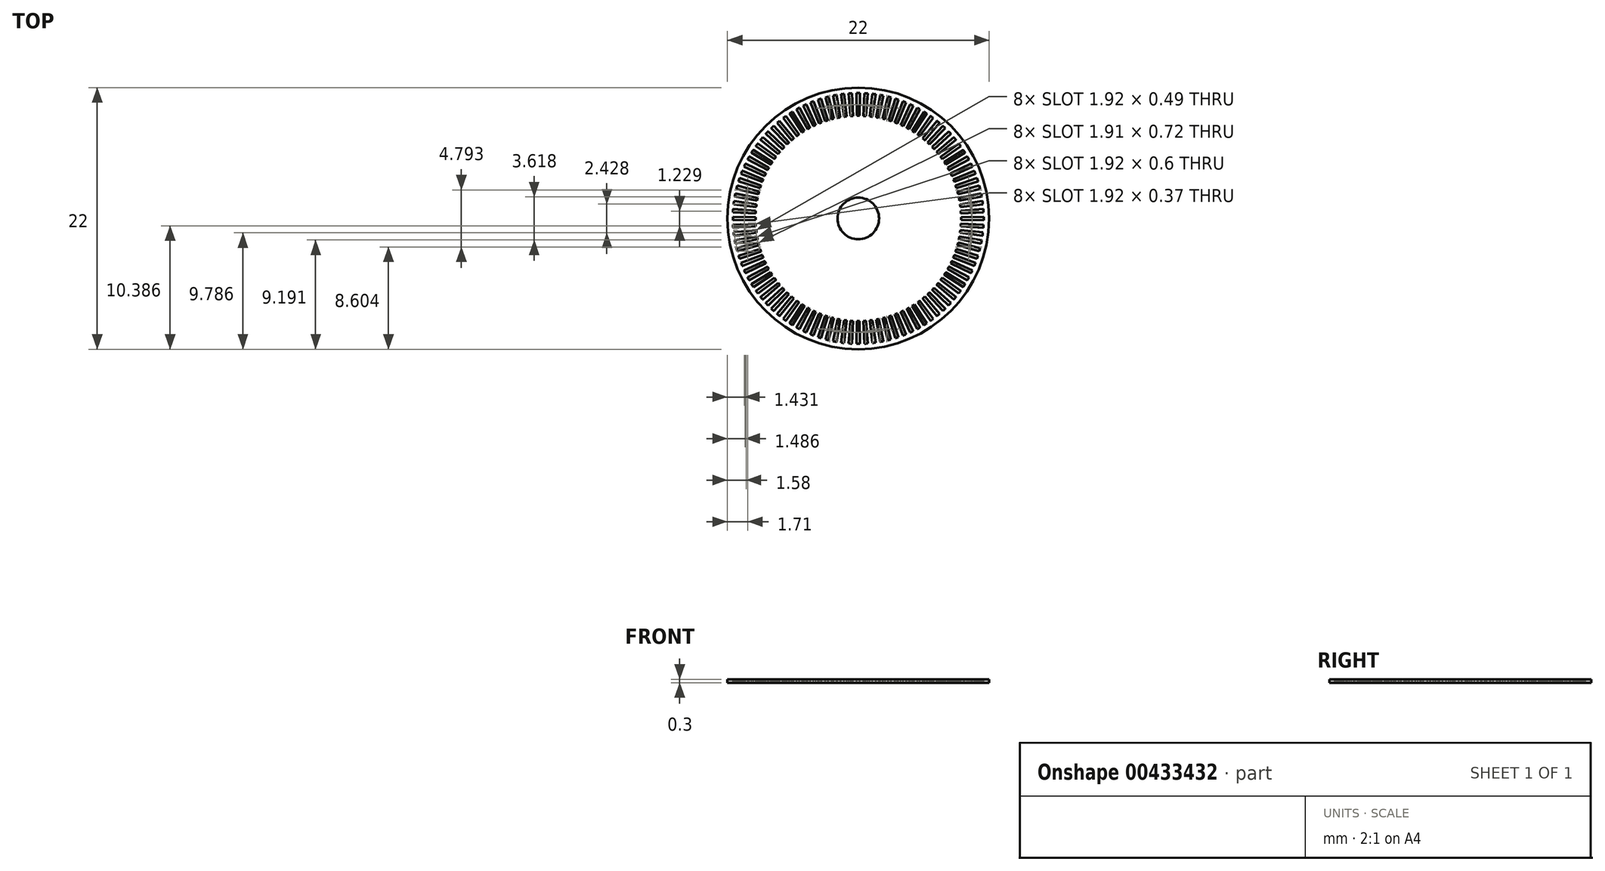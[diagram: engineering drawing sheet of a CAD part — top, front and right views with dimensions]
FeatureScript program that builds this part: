
annotation { "Feature Type Name" : "Feature", "Feature Type Description" : "" }
export const myFeature = defineFeature(function(context is Context, id is Id, definition is map)
    precondition{}
    {
        {
            var Q0;
            Q0=qCreatedBy(makeId("Top.planeOp"),FACE);
            var sketch = newSketch(context, id + "F0", { "sketchPlane" : qUnion([Q0])});
            skCircle(sketch, "E0", {"center": v(0, 0) * mm, "radius": 11 * mm});
            skSolve(sketch);
        }
        {
            var Q0;
            Q0=makeQuery(id+"F0.imprint","IMPRINT",FACE,{"disambiguationData":[TD([[makeQuery(id+"F0.imprint","IMPRINT",EDGE,{"derivedFrom":sQuery(id+"F0.wireOp",EDGE,"E0")}),1.0]])]});
            extrude(context, id + "F1", {"entities" : qUnion([Q0]), "oppositeDirection" : true, "depth" : .3 * mm});
        }
        {
            var Q0;
            Q0=sQuery(id+"F0.wireOp",VERTEX,"E0.center");
            var Q1;
            Q1=makeQuery(id+"F1.opExtrude","SWEPT_BODY",BODY,{"disambiguationData":[OSD([sQuery(id+"F0.wireOp",EDGE,"E0")])]});
            hole(context, id + "F2", {"style" : HoleStyle.SIMPLE, "endStyle" : HoleEndStyle.THROUGH, "holeDiameter" : 3.5 * mm, "isTappedThrough" : true, "tappedDepth" : 12.7 * mm, "tapClearance" : 3, "locations" : qUnion([Q0]), "scope" : qUnion([Q1])});
        }
        {
            var Q0;
            Q0=qCreatedBy(makeId("Top.planeOp"),FACE);
            var sketch = newSketch(context, id + "F3", { "sketchPlane" : qUnion([Q0])});
            skLineSegment(sketch, "E1", {"start": v(0, 0) * mm, "end": v(11, 0) * mm, "construction": true});
            skLineSegment(sketch, "E2", {"start": v(8.64, -0.11) * mm, "end": v(10.54, -0.14) * mm});
            skArc(sketch, "E3", {"start": v(10.54, -0.14) * mm, "mid": v(10.54, 0) * mm, "end": v(10.54, 0.14) * mm});
            skArc(sketch, "E4", {"start": v(8.64, -0.11) * mm, "mid": v(8.64, 0) * mm, "end": v(8.64, 0.11) * mm});
            skLineSegment(sketch, "E5.MirrorCS", {"start": v(8.64, 0.11) * mm, "end": v(10.54, 0.14) * mm});
            skArc(sketch, "E6.1.0", {"start": v(8.63, 0.43) * mm, "mid": v(8.62, 0.54) * mm, "end": v(8.61, 0.66) * mm});
            skLineSegment(sketch, "E6.1.1", {"start": v(8.61, 0.66) * mm, "end": v(10.51, 0.8) * mm});
            skArc(sketch, "E6.1.2", {"start": v(10.53, 0.52) * mm, "mid": v(10.52, 0.66) * mm, "end": v(10.51, 0.8) * mm});
            skLineSegment(sketch, "E6.1.3", {"start": v(8.63, 0.43) * mm, "end": v(10.53, 0.52) * mm});
            skArc(sketch, "E6.2.0", {"start": v(8.58, 0.97) * mm, "mid": v(8.57, 1.08) * mm, "end": v(8.55, 1.2) * mm});
            skLineSegment(sketch, "E6.2.1", {"start": v(8.55, 1.2) * mm, "end": v(10.44, 1.46) * mm});
            skArc(sketch, "E6.2.2", {"start": v(10.47, 1.18) * mm, "mid": v(10.46, 1.32) * mm, "end": v(10.44, 1.46) * mm});
            skLineSegment(sketch, "E6.2.3", {"start": v(8.58, 0.97) * mm, "end": v(10.47, 1.18) * mm});
            skArc(sketch, "E6.3.0", {"start": v(8.5, 1.5) * mm, "mid": v(8.48, 1.62) * mm, "end": v(8.46, 1.73) * mm});
            skLineSegment(sketch, "E6.3.1", {"start": v(8.46, 1.73) * mm, "end": v(10.33, 2.11) * mm});
            skArc(sketch, "E6.3.2", {"start": v(10.38, 1.84) * mm, "mid": v(10.35, 1.98) * mm, "end": v(10.33, 2.11) * mm});
            skLineSegment(sketch, "E6.3.3", {"start": v(8.5, 1.5) * mm, "end": v(10.38, 1.84) * mm});
            skArc(sketch, "E6.4.0", {"start": v(8.4, 2.04) * mm, "mid": v(8.36, 2.15) * mm, "end": v(8.34, 2.26) * mm});
            skLineSegment(sketch, "E6.4.1", {"start": v(8.34, 2.26) * mm, "end": v(10.17, 2.75) * mm});
            skArc(sketch, "E6.4.2", {"start": v(10.24, 2.49) * mm, "mid": v(10.2, 2.62) * mm, "end": v(10.17, 2.75) * mm});
            skLineSegment(sketch, "E6.4.3", {"start": v(8.4, 2.04) * mm, "end": v(10.24, 2.49) * mm});
            skArc(sketch, "E6.5.0", {"start": v(8.25, 2.56) * mm, "mid": v(8.21, 2.67) * mm, "end": v(8.18, 2.78) * mm});
            skLineSegment(sketch, "E6.5.1", {"start": v(8.18, 2.78) * mm, "end": v(9.98, 3.39) * mm});
            skArc(sketch, "E6.5.2", {"start": v(10.07, 3.13) * mm, "mid": v(10.03, 3.26) * mm, "end": v(9.98, 3.39) * mm});
            skLineSegment(sketch, "E6.5.3", {"start": v(8.25, 2.56) * mm, "end": v(10.07, 3.13) * mm});
            skArc(sketch, "E6.6.0", {"start": v(8.07, 3.07) * mm, "mid": v(8.03, 3.18) * mm, "end": v(7.99, 3.28) * mm});
            skLineSegment(sketch, "E6.6.1", {"start": v(7.99, 3.28) * mm, "end": v(9.75, 4) * mm});
            skArc(sketch, "E6.6.2", {"start": v(9.85, 3.75) * mm, "mid": v(9.8, 3.88) * mm, "end": v(9.75, 4) * mm});
            skLineSegment(sketch, "E6.6.3", {"start": v(8.07, 3.07) * mm, "end": v(9.85, 3.75) * mm});
            skArc(sketch, "E6.7.0", {"start": v(7.86, 3.57) * mm, "mid": v(7.81, 3.68) * mm, "end": v(7.77, 3.78) * mm});
            skLineSegment(sketch, "E6.7.1", {"start": v(7.77, 3.78) * mm, "end": v(9.48, 4.61) * mm});
            skArc(sketch, "E6.7.2", {"start": v(9.6, 4.36) * mm, "mid": v(9.54, 4.49) * mm, "end": v(9.48, 4.61) * mm});
            skLineSegment(sketch, "E6.7.3", {"start": v(7.86, 3.57) * mm, "end": v(9.6, 4.36) * mm});
            skArc(sketch, "E6.8.0", {"start": v(7.62, 4.06) * mm, "mid": v(7.57, 4.16) * mm, "end": v(7.51, 4.26) * mm});
            skLineSegment(sketch, "E6.8.1", {"start": v(7.51, 4.26) * mm, "end": v(9.17, 5.2) * mm});
            skArc(sketch, "E6.8.2", {"start": v(9.3, 4.96) * mm, "mid": v(9.24, 5.08) * mm, "end": v(9.17, 5.2) * mm});
            skLineSegment(sketch, "E6.8.3", {"start": v(7.62, 4.06) * mm, "end": v(9.3, 4.96) * mm});
            skArc(sketch, "E6.9.0", {"start": v(7.35, 4.53) * mm, "mid": v(7.3, 4.63) * mm, "end": v(7.23, 4.72) * mm});
            skLineSegment(sketch, "E6.9.1", {"start": v(7.23, 4.72) * mm, "end": v(8.83, 5.76) * mm});
            skArc(sketch, "E6.9.2", {"start": v(8.97, 5.53) * mm, "mid": v(8.9, 5.65) * mm, "end": v(8.83, 5.76) * mm});
            skLineSegment(sketch, "E6.9.3", {"start": v(7.35, 4.53) * mm, "end": v(8.97, 5.53) * mm});
            skArc(sketch, "E6.10.0", {"start": v(7.05, 4.98) * mm, "mid": v(6.99, 5.08) * mm, "end": v(6.92, 5.17) * mm});
            skLineSegment(sketch, "E6.10.1", {"start": v(6.92, 5.17) * mm, "end": v(8.45, 6.3) * mm});
            skArc(sketch, "E6.10.2", {"start": v(8.6, 6.08) * mm, "mid": v(8.53, 6.2) * mm, "end": v(8.45, 6.3) * mm});
            skLineSegment(sketch, "E6.10.3", {"start": v(7.05, 4.98) * mm, "end": v(8.6, 6.08) * mm});
            skArc(sketch, "E6.11.0", {"start": v(6.73, 5.42) * mm, "mid": v(6.65, 5.5) * mm, "end": v(6.58, 5.6) * mm});
            skLineSegment(sketch, "E6.11.1", {"start": v(6.58, 5.6) * mm, "end": v(8.03, 6.82) * mm});
            skArc(sketch, "E6.11.2", {"start": v(8.2, 6.61) * mm, "mid": v(8.12, 6.72) * mm, "end": v(8.03, 6.82) * mm});
            skLineSegment(sketch, "E6.11.3", {"start": v(6.73, 5.42) * mm, "end": v(8.2, 6.61) * mm});
            skArc(sketch, "E6.12.0", {"start": v(6.37, 5.83) * mm, "mid": v(6.3, 5.91) * mm, "end": v(6.22, 6) * mm});
            skLineSegment(sketch, "E6.12.1", {"start": v(6.22, 6) * mm, "end": v(7.59, 7.32) * mm});
            skArc(sketch, "E6.12.2", {"start": v(7.78, 7.11) * mm, "mid": v(7.68, 7.22) * mm, "end": v(7.59, 7.32) * mm});
            skLineSegment(sketch, "E6.12.3", {"start": v(6.37, 5.83) * mm, "end": v(7.78, 7.11) * mm});
            skArc(sketch, "E6.13.0", {"start": v(6, 6.22) * mm, "mid": v(5.91, 6.3) * mm, "end": v(5.83, 6.37) * mm});
            skLineSegment(sketch, "E6.13.1", {"start": v(5.83, 6.37) * mm, "end": v(7.11, 7.78) * mm});
            skArc(sketch, "E6.13.2", {"start": v(7.32, 7.59) * mm, "mid": v(7.22, 7.68) * mm, "end": v(7.11, 7.78) * mm});
            skLineSegment(sketch, "E6.13.3", {"start": v(6, 6.22) * mm, "end": v(7.32, 7.59) * mm});
            skArc(sketch, "E6.14.0", {"start": v(5.6, 6.58) * mm, "mid": v(5.5, 6.65) * mm, "end": v(5.42, 6.73) * mm});
            skLineSegment(sketch, "E6.14.1", {"start": v(5.42, 6.73) * mm, "end": v(6.61, 8.2) * mm});
            skArc(sketch, "E6.14.2", {"start": v(6.82, 8.03) * mm, "mid": v(6.72, 8.12) * mm, "end": v(6.61, 8.2) * mm});
            skLineSegment(sketch, "E6.14.3", {"start": v(5.6, 6.58) * mm, "end": v(6.82, 8.03) * mm});
            skArc(sketch, "E6.15.0", {"start": v(5.17, 6.92) * mm, "mid": v(5.08, 6.99) * mm, "end": v(4.98, 7.05) * mm});
            skLineSegment(sketch, "E6.15.1", {"start": v(4.98, 7.05) * mm, "end": v(6.08, 8.6) * mm});
            skArc(sketch, "E6.15.2", {"start": v(6.3, 8.45) * mm, "mid": v(6.2, 8.53) * mm, "end": v(6.08, 8.6) * mm});
            skLineSegment(sketch, "E6.15.3", {"start": v(5.17, 6.92) * mm, "end": v(6.3, 8.45) * mm});
            skArc(sketch, "E6.16.0", {"start": v(4.72, 7.23) * mm, "mid": v(4.63, 7.3) * mm, "end": v(4.53, 7.35) * mm});
            skLineSegment(sketch, "E6.16.1", {"start": v(4.53, 7.35) * mm, "end": v(5.53, 8.97) * mm});
            skArc(sketch, "E6.16.2", {"start": v(5.76, 8.83) * mm, "mid": v(5.65, 8.9) * mm, "end": v(5.53, 8.97) * mm});
            skLineSegment(sketch, "E6.16.3", {"start": v(4.72, 7.23) * mm, "end": v(5.76, 8.83) * mm});
            skArc(sketch, "E6.17.0", {"start": v(4.26, 7.51) * mm, "mid": v(4.16, 7.57) * mm, "end": v(4.06, 7.62) * mm});
            skLineSegment(sketch, "E6.17.1", {"start": v(4.06, 7.62) * mm, "end": v(4.96, 9.3) * mm});
            skArc(sketch, "E6.17.2", {"start": v(5.2, 9.17) * mm, "mid": v(5.08, 9.24) * mm, "end": v(4.96, 9.3) * mm});
            skLineSegment(sketch, "E6.17.3", {"start": v(4.26, 7.51) * mm, "end": v(5.2, 9.17) * mm});
            skArc(sketch, "E6.18.0", {"start": v(3.78, 7.77) * mm, "mid": v(3.68, 7.81) * mm, "end": v(3.57, 7.86) * mm});
            skLineSegment(sketch, "E6.18.1", {"start": v(3.57, 7.86) * mm, "end": v(4.36, 9.6) * mm});
            skArc(sketch, "E6.18.2", {"start": v(4.61, 9.48) * mm, "mid": v(4.49, 9.54) * mm, "end": v(4.36, 9.6) * mm});
            skLineSegment(sketch, "E6.18.3", {"start": v(3.78, 7.77) * mm, "end": v(4.61, 9.48) * mm});
            skArc(sketch, "E6.19.0", {"start": v(3.28, 7.99) * mm, "mid": v(3.18, 8.03) * mm, "end": v(3.07, 8.07) * mm});
            skLineSegment(sketch, "E6.19.1", {"start": v(3.07, 8.07) * mm, "end": v(3.75, 9.85) * mm});
            skArc(sketch, "E6.19.2", {"start": v(4, 9.75) * mm, "mid": v(3.88, 9.8) * mm, "end": v(3.75, 9.85) * mm});
            skLineSegment(sketch, "E6.19.3", {"start": v(3.28, 7.99) * mm, "end": v(4, 9.75) * mm});
            skArc(sketch, "E6.20.0", {"start": v(2.78, 8.18) * mm, "mid": v(2.67, 8.21) * mm, "end": v(2.56, 8.25) * mm});
            skLineSegment(sketch, "E6.20.1", {"start": v(2.56, 8.25) * mm, "end": v(3.13, 10.07) * mm});
            skArc(sketch, "E6.20.2", {"start": v(3.39, 9.98) * mm, "mid": v(3.26, 10.03) * mm, "end": v(3.13, 10.07) * mm});
            skLineSegment(sketch, "E6.20.3", {"start": v(2.78, 8.18) * mm, "end": v(3.39, 9.98) * mm});
            skArc(sketch, "E6.21.0", {"start": v(2.26, 8.34) * mm, "mid": v(2.15, 8.36) * mm, "end": v(2.04, 8.4) * mm});
            skLineSegment(sketch, "E6.21.1", {"start": v(2.04, 8.4) * mm, "end": v(2.49, 10.24) * mm});
            skArc(sketch, "E6.21.2", {"start": v(2.75, 10.17) * mm, "mid": v(2.62, 10.2) * mm, "end": v(2.49, 10.24) * mm});
            skLineSegment(sketch, "E6.21.3", {"start": v(2.26, 8.34) * mm, "end": v(2.75, 10.17) * mm});
            skArc(sketch, "E6.22.0", {"start": v(1.73, 8.46) * mm, "mid": v(1.62, 8.48) * mm, "end": v(1.5, 8.5) * mm});
            skLineSegment(sketch, "E6.22.1", {"start": v(1.5, 8.5) * mm, "end": v(1.84, 10.38) * mm});
            skArc(sketch, "E6.22.2", {"start": v(2.11, 10.33) * mm, "mid": v(1.98, 10.35) * mm, "end": v(1.84, 10.38) * mm});
            skLineSegment(sketch, "E6.22.3", {"start": v(1.73, 8.46) * mm, "end": v(2.11, 10.33) * mm});
            skArc(sketch, "E6.23.0", {"start": v(1.2, 8.55) * mm, "mid": v(1.08, 8.57) * mm, "end": v(0.97, 8.58) * mm});
            skLineSegment(sketch, "E6.23.1", {"start": v(0.97, 8.58) * mm, "end": v(1.18, 10.47) * mm});
            skArc(sketch, "E6.23.2", {"start": v(1.46, 10.44) * mm, "mid": v(1.32, 10.46) * mm, "end": v(1.18, 10.47) * mm});
            skLineSegment(sketch, "E6.23.3", {"start": v(1.2, 8.55) * mm, "end": v(1.46, 10.44) * mm});
            skArc(sketch, "E6.24.0", {"start": v(0.66, 8.61) * mm, "mid": v(0.54, 8.62) * mm, "end": v(0.43, 8.63) * mm});
            skLineSegment(sketch, "E6.24.1", {"start": v(0.43, 8.63) * mm, "end": v(0.52, 10.53) * mm});
            skArc(sketch, "E6.24.2", {"start": v(0.8, 10.51) * mm, "mid": v(0.66, 10.52) * mm, "end": v(0.52, 10.53) * mm});
            skLineSegment(sketch, "E6.24.3", {"start": v(0.66, 8.61) * mm, "end": v(0.8, 10.51) * mm});
            skArc(sketch, "E6.25.0", {"start": v(0.11, 8.64) * mm, "mid": v(0, 8.64) * mm, "end": v(-0.11, 8.64) * mm});
            skLineSegment(sketch, "E6.25.1", {"start": v(-0.11, 8.64) * mm, "end": v(-0.14, 10.54) * mm});
            skArc(sketch, "E6.25.2", {"start": v(0.14, 10.54) * mm, "mid": v(0, 10.54) * mm, "end": v(-0.14, 10.54) * mm});
            skLineSegment(sketch, "E6.25.3", {"start": v(0.11, 8.64) * mm, "end": v(0.14, 10.54) * mm});
            skArc(sketch, "E6.26.0", {"start": v(-0.43, 8.63) * mm, "mid": v(-0.54, 8.62) * mm, "end": v(-0.66, 8.61) * mm});
            skLineSegment(sketch, "E6.26.1", {"start": v(-0.66, 8.61) * mm, "end": v(-0.8, 10.51) * mm});
            skArc(sketch, "E6.26.2", {"start": v(-0.52, 10.53) * mm, "mid": v(-0.66, 10.52) * mm, "end": v(-0.8, 10.51) * mm});
            skLineSegment(sketch, "E6.26.3", {"start": v(-0.43, 8.63) * mm, "end": v(-0.52, 10.53) * mm});
            skArc(sketch, "E6.27.0", {"start": v(-0.97, 8.58) * mm, "mid": v(-1.08, 8.57) * mm, "end": v(-1.2, 8.55) * mm});
            skLineSegment(sketch, "E6.27.1", {"start": v(-1.2, 8.55) * mm, "end": v(-1.46, 10.44) * mm});
            skArc(sketch, "E6.27.2", {"start": v(-1.18, 10.47) * mm, "mid": v(-1.32, 10.46) * mm, "end": v(-1.46, 10.44) * mm});
            skLineSegment(sketch, "E6.27.3", {"start": v(-0.97, 8.58) * mm, "end": v(-1.18, 10.47) * mm});
            skArc(sketch, "E6.28.0", {"start": v(-1.5, 8.5) * mm, "mid": v(-1.62, 8.48) * mm, "end": v(-1.73, 8.46) * mm});
            skLineSegment(sketch, "E6.28.1", {"start": v(-1.73, 8.46) * mm, "end": v(-2.11, 10.33) * mm});
            skArc(sketch, "E6.28.2", {"start": v(-1.84, 10.38) * mm, "mid": v(-1.98, 10.35) * mm, "end": v(-2.11, 10.33) * mm});
            skLineSegment(sketch, "E6.28.3", {"start": v(-1.5, 8.5) * mm, "end": v(-1.84, 10.38) * mm});
            skArc(sketch, "E6.29.0", {"start": v(-2.04, 8.4) * mm, "mid": v(-2.15, 8.36) * mm, "end": v(-2.26, 8.34) * mm});
            skLineSegment(sketch, "E6.29.1", {"start": v(-2.26, 8.34) * mm, "end": v(-2.75, 10.17) * mm});
            skArc(sketch, "E6.29.2", {"start": v(-2.49, 10.24) * mm, "mid": v(-2.62, 10.2) * mm, "end": v(-2.75, 10.17) * mm});
            skLineSegment(sketch, "E6.29.3", {"start": v(-2.04, 8.4) * mm, "end": v(-2.49, 10.24) * mm});
            skArc(sketch, "E6.30.0", {"start": v(-2.56, 8.25) * mm, "mid": v(-2.67, 8.21) * mm, "end": v(-2.78, 8.18) * mm});
            skLineSegment(sketch, "E6.30.1", {"start": v(-2.78, 8.18) * mm, "end": v(-3.39, 9.98) * mm});
            skArc(sketch, "E6.30.2", {"start": v(-3.13, 10.07) * mm, "mid": v(-3.26, 10.03) * mm, "end": v(-3.39, 9.98) * mm});
            skLineSegment(sketch, "E6.30.3", {"start": v(-2.56, 8.25) * mm, "end": v(-3.13, 10.07) * mm});
            skArc(sketch, "E6.31.0", {"start": v(-3.07, 8.07) * mm, "mid": v(-3.18, 8.03) * mm, "end": v(-3.28, 7.99) * mm});
            skLineSegment(sketch, "E6.31.1", {"start": v(-3.28, 7.99) * mm, "end": v(-4, 9.75) * mm});
            skArc(sketch, "E6.31.2", {"start": v(-3.75, 9.85) * mm, "mid": v(-3.88, 9.8) * mm, "end": v(-4, 9.75) * mm});
            skLineSegment(sketch, "E6.31.3", {"start": v(-3.07, 8.07) * mm, "end": v(-3.75, 9.85) * mm});
            skArc(sketch, "E6.32.0", {"start": v(-3.57, 7.86) * mm, "mid": v(-3.68, 7.81) * mm, "end": v(-3.78, 7.77) * mm});
            skLineSegment(sketch, "E6.32.1", {"start": v(-3.78, 7.77) * mm, "end": v(-4.61, 9.48) * mm});
            skArc(sketch, "E6.32.2", {"start": v(-4.36, 9.6) * mm, "mid": v(-4.49, 9.54) * mm, "end": v(-4.61, 9.48) * mm});
            skLineSegment(sketch, "E6.32.3", {"start": v(-3.57, 7.86) * mm, "end": v(-4.36, 9.6) * mm});
            skArc(sketch, "E6.33.0", {"start": v(-4.06, 7.62) * mm, "mid": v(-4.16, 7.57) * mm, "end": v(-4.26, 7.51) * mm});
            skLineSegment(sketch, "E6.33.1", {"start": v(-4.26, 7.51) * mm, "end": v(-5.2, 9.17) * mm});
            skArc(sketch, "E6.33.2", {"start": v(-4.96, 9.3) * mm, "mid": v(-5.08, 9.24) * mm, "end": v(-5.2, 9.17) * mm});
            skLineSegment(sketch, "E6.33.3", {"start": v(-4.06, 7.62) * mm, "end": v(-4.96, 9.3) * mm});
            skArc(sketch, "E6.34.0", {"start": v(-4.53, 7.35) * mm, "mid": v(-4.63, 7.3) * mm, "end": v(-4.72, 7.23) * mm});
            skLineSegment(sketch, "E6.34.1", {"start": v(-4.72, 7.23) * mm, "end": v(-5.76, 8.83) * mm});
            skArc(sketch, "E6.34.2", {"start": v(-5.53, 8.97) * mm, "mid": v(-5.65, 8.9) * mm, "end": v(-5.76, 8.83) * mm});
            skLineSegment(sketch, "E6.34.3", {"start": v(-4.53, 7.35) * mm, "end": v(-5.53, 8.97) * mm});
            skArc(sketch, "E6.35.0", {"start": v(-4.98, 7.05) * mm, "mid": v(-5.08, 6.99) * mm, "end": v(-5.17, 6.92) * mm});
            skLineSegment(sketch, "E6.35.1", {"start": v(-5.17, 6.92) * mm, "end": v(-6.3, 8.45) * mm});
            skArc(sketch, "E6.35.2", {"start": v(-6.08, 8.6) * mm, "mid": v(-6.2, 8.53) * mm, "end": v(-6.3, 8.45) * mm});
            skLineSegment(sketch, "E6.35.3", {"start": v(-4.98, 7.05) * mm, "end": v(-6.08, 8.6) * mm});
            skArc(sketch, "E6.36.0", {"start": v(-5.42, 6.73) * mm, "mid": v(-5.5, 6.65) * mm, "end": v(-5.6, 6.58) * mm});
            skLineSegment(sketch, "E6.36.1", {"start": v(-5.6, 6.58) * mm, "end": v(-6.82, 8.03) * mm});
            skArc(sketch, "E6.36.2", {"start": v(-6.61, 8.2) * mm, "mid": v(-6.72, 8.12) * mm, "end": v(-6.82, 8.03) * mm});
            skLineSegment(sketch, "E6.36.3", {"start": v(-5.42, 6.73) * mm, "end": v(-6.61, 8.2) * mm});
            skArc(sketch, "E6.37.0", {"start": v(-5.83, 6.37) * mm, "mid": v(-5.91, 6.3) * mm, "end": v(-6, 6.22) * mm});
            skLineSegment(sketch, "E6.37.1", {"start": v(-6, 6.22) * mm, "end": v(-7.32, 7.59) * mm});
            skArc(sketch, "E6.37.2", {"start": v(-7.11, 7.78) * mm, "mid": v(-7.22, 7.68) * mm, "end": v(-7.32, 7.59) * mm});
            skLineSegment(sketch, "E6.37.3", {"start": v(-5.83, 6.37) * mm, "end": v(-7.11, 7.78) * mm});
            skArc(sketch, "E6.38.0", {"start": v(-6.22, 6) * mm, "mid": v(-6.3, 5.91) * mm, "end": v(-6.37, 5.83) * mm});
            skLineSegment(sketch, "E6.38.1", {"start": v(-6.37, 5.83) * mm, "end": v(-7.78, 7.11) * mm});
            skArc(sketch, "E6.38.2", {"start": v(-7.59, 7.32) * mm, "mid": v(-7.68, 7.22) * mm, "end": v(-7.78, 7.11) * mm});
            skLineSegment(sketch, "E6.38.3", {"start": v(-6.22, 6) * mm, "end": v(-7.59, 7.32) * mm});
            skArc(sketch, "E6.39.0", {"start": v(-6.58, 5.6) * mm, "mid": v(-6.65, 5.5) * mm, "end": v(-6.73, 5.42) * mm});
            skLineSegment(sketch, "E6.39.1", {"start": v(-6.73, 5.42) * mm, "end": v(-8.2, 6.61) * mm});
            skArc(sketch, "E6.39.2", {"start": v(-8.03, 6.82) * mm, "mid": v(-8.12, 6.72) * mm, "end": v(-8.2, 6.61) * mm});
            skLineSegment(sketch, "E6.39.3", {"start": v(-6.58, 5.6) * mm, "end": v(-8.03, 6.82) * mm});
            skArc(sketch, "E6.40.0", {"start": v(-6.92, 5.17) * mm, "mid": v(-6.99, 5.08) * mm, "end": v(-7.05, 4.98) * mm});
            skLineSegment(sketch, "E6.40.1", {"start": v(-7.05, 4.98) * mm, "end": v(-8.6, 6.08) * mm});
            skArc(sketch, "E6.40.2", {"start": v(-8.45, 6.3) * mm, "mid": v(-8.53, 6.2) * mm, "end": v(-8.6, 6.08) * mm});
            skLineSegment(sketch, "E6.40.3", {"start": v(-6.92, 5.17) * mm, "end": v(-8.45, 6.3) * mm});
            skArc(sketch, "E6.41.0", {"start": v(-7.23, 4.72) * mm, "mid": v(-7.3, 4.63) * mm, "end": v(-7.35, 4.53) * mm});
            skLineSegment(sketch, "E6.41.1", {"start": v(-7.35, 4.53) * mm, "end": v(-8.97, 5.53) * mm});
            skArc(sketch, "E6.41.2", {"start": v(-8.83, 5.76) * mm, "mid": v(-8.9, 5.65) * mm, "end": v(-8.97, 5.53) * mm});
            skLineSegment(sketch, "E6.41.3", {"start": v(-7.23, 4.72) * mm, "end": v(-8.83, 5.76) * mm});
            skArc(sketch, "E6.42.0", {"start": v(-7.51, 4.26) * mm, "mid": v(-7.57, 4.16) * mm, "end": v(-7.62, 4.06) * mm});
            skLineSegment(sketch, "E6.42.1", {"start": v(-7.62, 4.06) * mm, "end": v(-9.3, 4.96) * mm});
            skArc(sketch, "E6.42.2", {"start": v(-9.17, 5.2) * mm, "mid": v(-9.24, 5.08) * mm, "end": v(-9.3, 4.96) * mm});
            skLineSegment(sketch, "E6.42.3", {"start": v(-7.51, 4.26) * mm, "end": v(-9.17, 5.2) * mm});
            skArc(sketch, "E6.43.0", {"start": v(-7.77, 3.78) * mm, "mid": v(-7.81, 3.68) * mm, "end": v(-7.86, 3.57) * mm});
            skLineSegment(sketch, "E6.43.1", {"start": v(-7.86, 3.57) * mm, "end": v(-9.6, 4.36) * mm});
            skArc(sketch, "E6.43.2", {"start": v(-9.48, 4.61) * mm, "mid": v(-9.54, 4.49) * mm, "end": v(-9.6, 4.36) * mm});
            skLineSegment(sketch, "E6.43.3", {"start": v(-7.77, 3.78) * mm, "end": v(-9.48, 4.61) * mm});
            skArc(sketch, "E6.44.0", {"start": v(-7.99, 3.28) * mm, "mid": v(-8.03, 3.18) * mm, "end": v(-8.07, 3.07) * mm});
            skLineSegment(sketch, "E6.44.1", {"start": v(-8.07, 3.07) * mm, "end": v(-9.85, 3.75) * mm});
            skArc(sketch, "E6.44.2", {"start": v(-9.75, 4) * mm, "mid": v(-9.8, 3.88) * mm, "end": v(-9.85, 3.75) * mm});
            skLineSegment(sketch, "E6.44.3", {"start": v(-7.99, 3.28) * mm, "end": v(-9.75, 4) * mm});
            skArc(sketch, "E6.45.0", {"start": v(-8.18, 2.78) * mm, "mid": v(-8.21, 2.67) * mm, "end": v(-8.25, 2.56) * mm});
            skLineSegment(sketch, "E6.45.1", {"start": v(-8.25, 2.56) * mm, "end": v(-10.07, 3.13) * mm});
            skArc(sketch, "E6.45.2", {"start": v(-9.98, 3.39) * mm, "mid": v(-10.03, 3.26) * mm, "end": v(-10.07, 3.13) * mm});
            skLineSegment(sketch, "E6.45.3", {"start": v(-8.18, 2.78) * mm, "end": v(-9.98, 3.39) * mm});
            skArc(sketch, "E6.46.0", {"start": v(-8.34, 2.26) * mm, "mid": v(-8.36, 2.15) * mm, "end": v(-8.4, 2.04) * mm});
            skLineSegment(sketch, "E6.46.1", {"start": v(-8.4, 2.04) * mm, "end": v(-10.24, 2.49) * mm});
            skArc(sketch, "E6.46.2", {"start": v(-10.17, 2.75) * mm, "mid": v(-10.2, 2.62) * mm, "end": v(-10.24, 2.49) * mm});
            skLineSegment(sketch, "E6.46.3", {"start": v(-8.34, 2.26) * mm, "end": v(-10.17, 2.75) * mm});
            skArc(sketch, "E6.47.0", {"start": v(-8.46, 1.73) * mm, "mid": v(-8.48, 1.62) * mm, "end": v(-8.5, 1.5) * mm});
            skLineSegment(sketch, "E6.47.1", {"start": v(-8.5, 1.5) * mm, "end": v(-10.38, 1.84) * mm});
            skArc(sketch, "E6.47.2", {"start": v(-10.33, 2.11) * mm, "mid": v(-10.35, 1.98) * mm, "end": v(-10.38, 1.84) * mm});
            skLineSegment(sketch, "E6.47.3", {"start": v(-8.46, 1.73) * mm, "end": v(-10.33, 2.11) * mm});
            skArc(sketch, "E6.48.0", {"start": v(-8.55, 1.2) * mm, "mid": v(-8.57, 1.08) * mm, "end": v(-8.58, 0.97) * mm});
            skLineSegment(sketch, "E6.48.1", {"start": v(-8.58, 0.97) * mm, "end": v(-10.47, 1.18) * mm});
            skArc(sketch, "E6.48.2", {"start": v(-10.44, 1.46) * mm, "mid": v(-10.46, 1.32) * mm, "end": v(-10.47, 1.18) * mm});
            skLineSegment(sketch, "E6.48.3", {"start": v(-8.55, 1.2) * mm, "end": v(-10.44, 1.46) * mm});
            skArc(sketch, "E6.49.0", {"start": v(-8.61, 0.66) * mm, "mid": v(-8.62, 0.54) * mm, "end": v(-8.63, 0.43) * mm});
            skLineSegment(sketch, "E6.49.1", {"start": v(-8.63, 0.43) * mm, "end": v(-10.53, 0.52) * mm});
            skArc(sketch, "E6.49.2", {"start": v(-10.51, 0.8) * mm, "mid": v(-10.52, 0.66) * mm, "end": v(-10.53, 0.52) * mm});
            skLineSegment(sketch, "E6.49.3", {"start": v(-8.61, 0.66) * mm, "end": v(-10.51, 0.8) * mm});
            skArc(sketch, "E6.50.0", {"start": v(-8.64, 0.11) * mm, "mid": v(-8.64, 0) * mm, "end": v(-8.64, -0.11) * mm});
            skLineSegment(sketch, "E6.50.1", {"start": v(-8.64, -0.11) * mm, "end": v(-10.54, -0.14) * mm});
            skArc(sketch, "E6.50.2", {"start": v(-10.54, 0.14) * mm, "mid": v(-10.54, 0) * mm, "end": v(-10.54, -0.14) * mm});
            skLineSegment(sketch, "E6.50.3", {"start": v(-8.64, 0.11) * mm, "end": v(-10.54, 0.14) * mm});
            skArc(sketch, "E6.51.0", {"start": v(-8.63, -0.43) * mm, "mid": v(-8.62, -0.54) * mm, "end": v(-8.61, -0.66) * mm});
            skLineSegment(sketch, "E6.51.1", {"start": v(-8.61, -0.66) * mm, "end": v(-10.51, -0.8) * mm});
            skArc(sketch, "E6.51.2", {"start": v(-10.53, -0.52) * mm, "mid": v(-10.52, -0.66) * mm, "end": v(-10.51, -0.8) * mm});
            skLineSegment(sketch, "E6.51.3", {"start": v(-8.63, -0.43) * mm, "end": v(-10.53, -0.52) * mm});
            skArc(sketch, "E6.52.0", {"start": v(-8.58, -0.97) * mm, "mid": v(-8.57, -1.08) * mm, "end": v(-8.55, -1.2) * mm});
            skLineSegment(sketch, "E6.52.1", {"start": v(-8.55, -1.2) * mm, "end": v(-10.44, -1.46) * mm});
            skArc(sketch, "E6.52.2", {"start": v(-10.47, -1.18) * mm, "mid": v(-10.46, -1.32) * mm, "end": v(-10.44, -1.46) * mm});
            skLineSegment(sketch, "E6.52.3", {"start": v(-8.58, -0.97) * mm, "end": v(-10.47, -1.18) * mm});
            skArc(sketch, "E6.53.0", {"start": v(-8.5, -1.5) * mm, "mid": v(-8.48, -1.62) * mm, "end": v(-8.46, -1.73) * mm});
            skLineSegment(sketch, "E6.53.1", {"start": v(-8.46, -1.73) * mm, "end": v(-10.33, -2.11) * mm});
            skArc(sketch, "E6.53.2", {"start": v(-10.38, -1.84) * mm, "mid": v(-10.35, -1.98) * mm, "end": v(-10.33, -2.11) * mm});
            skLineSegment(sketch, "E6.53.3", {"start": v(-8.5, -1.5) * mm, "end": v(-10.38, -1.84) * mm});
            skArc(sketch, "E6.54.0", {"start": v(-8.4, -2.04) * mm, "mid": v(-8.36, -2.15) * mm, "end": v(-8.34, -2.26) * mm});
            skLineSegment(sketch, "E6.54.1", {"start": v(-8.34, -2.26) * mm, "end": v(-10.17, -2.75) * mm});
            skArc(sketch, "E6.54.2", {"start": v(-10.24, -2.49) * mm, "mid": v(-10.2, -2.62) * mm, "end": v(-10.17, -2.75) * mm});
            skLineSegment(sketch, "E6.54.3", {"start": v(-8.4, -2.04) * mm, "end": v(-10.24, -2.49) * mm});
            skArc(sketch, "E6.55.0", {"start": v(-8.25, -2.56) * mm, "mid": v(-8.21, -2.67) * mm, "end": v(-8.18, -2.78) * mm});
            skLineSegment(sketch, "E6.55.1", {"start": v(-8.18, -2.78) * mm, "end": v(-9.98, -3.39) * mm});
            skArc(sketch, "E6.55.2", {"start": v(-10.07, -3.13) * mm, "mid": v(-10.03, -3.26) * mm, "end": v(-9.98, -3.39) * mm});
            skLineSegment(sketch, "E6.55.3", {"start": v(-8.25, -2.56) * mm, "end": v(-10.07, -3.13) * mm});
            skArc(sketch, "E6.56.0", {"start": v(-8.07, -3.07) * mm, "mid": v(-8.03, -3.18) * mm, "end": v(-7.99, -3.28) * mm});
            skLineSegment(sketch, "E6.56.1", {"start": v(-7.99, -3.28) * mm, "end": v(-9.75, -4) * mm});
            skArc(sketch, "E6.56.2", {"start": v(-9.85, -3.75) * mm, "mid": v(-9.8, -3.88) * mm, "end": v(-9.75, -4) * mm});
            skLineSegment(sketch, "E6.56.3", {"start": v(-8.07, -3.07) * mm, "end": v(-9.85, -3.75) * mm});
            skArc(sketch, "E6.57.0", {"start": v(-7.86, -3.57) * mm, "mid": v(-7.81, -3.68) * mm, "end": v(-7.77, -3.78) * mm});
            skLineSegment(sketch, "E6.57.1", {"start": v(-7.77, -3.78) * mm, "end": v(-9.48, -4.61) * mm});
            skArc(sketch, "E6.57.2", {"start": v(-9.6, -4.36) * mm, "mid": v(-9.54, -4.49) * mm, "end": v(-9.48, -4.61) * mm});
            skLineSegment(sketch, "E6.57.3", {"start": v(-7.86, -3.57) * mm, "end": v(-9.6, -4.36) * mm});
            skArc(sketch, "E6.58.0", {"start": v(-7.62, -4.06) * mm, "mid": v(-7.57, -4.16) * mm, "end": v(-7.51, -4.26) * mm});
            skLineSegment(sketch, "E6.58.1", {"start": v(-7.51, -4.26) * mm, "end": v(-9.17, -5.2) * mm});
            skArc(sketch, "E6.58.2", {"start": v(-9.3, -4.96) * mm, "mid": v(-9.24, -5.08) * mm, "end": v(-9.17, -5.2) * mm});
            skLineSegment(sketch, "E6.58.3", {"start": v(-7.62, -4.06) * mm, "end": v(-9.3, -4.96) * mm});
            skArc(sketch, "E6.59.0", {"start": v(-7.35, -4.53) * mm, "mid": v(-7.3, -4.63) * mm, "end": v(-7.23, -4.72) * mm});
            skLineSegment(sketch, "E6.59.1", {"start": v(-7.23, -4.72) * mm, "end": v(-8.83, -5.76) * mm});
            skArc(sketch, "E6.59.2", {"start": v(-8.97, -5.53) * mm, "mid": v(-8.9, -5.65) * mm, "end": v(-8.83, -5.76) * mm});
            skLineSegment(sketch, "E6.59.3", {"start": v(-7.35, -4.53) * mm, "end": v(-8.97, -5.53) * mm});
            skArc(sketch, "E6.60.0", {"start": v(-7.05, -4.98) * mm, "mid": v(-6.99, -5.08) * mm, "end": v(-6.92, -5.17) * mm});
            skLineSegment(sketch, "E6.60.1", {"start": v(-6.92, -5.17) * mm, "end": v(-8.45, -6.3) * mm});
            skArc(sketch, "E6.60.2", {"start": v(-8.6, -6.08) * mm, "mid": v(-8.53, -6.2) * mm, "end": v(-8.45, -6.3) * mm});
            skLineSegment(sketch, "E6.60.3", {"start": v(-7.05, -4.98) * mm, "end": v(-8.6, -6.08) * mm});
            skArc(sketch, "E6.61.0", {"start": v(-6.73, -5.42) * mm, "mid": v(-6.65, -5.5) * mm, "end": v(-6.58, -5.6) * mm});
            skLineSegment(sketch, "E6.61.1", {"start": v(-6.58, -5.6) * mm, "end": v(-8.03, -6.82) * mm});
            skArc(sketch, "E6.61.2", {"start": v(-8.2, -6.61) * mm, "mid": v(-8.12, -6.72) * mm, "end": v(-8.03, -6.82) * mm});
            skLineSegment(sketch, "E6.61.3", {"start": v(-6.73, -5.42) * mm, "end": v(-8.2, -6.61) * mm});
            skArc(sketch, "E6.62.0", {"start": v(-6.37, -5.83) * mm, "mid": v(-6.3, -5.91) * mm, "end": v(-6.22, -6) * mm});
            skLineSegment(sketch, "E6.62.1", {"start": v(-6.22, -6) * mm, "end": v(-7.59, -7.32) * mm});
            skArc(sketch, "E6.62.2", {"start": v(-7.78, -7.11) * mm, "mid": v(-7.68, -7.22) * mm, "end": v(-7.59, -7.32) * mm});
            skLineSegment(sketch, "E6.62.3", {"start": v(-6.37, -5.83) * mm, "end": v(-7.78, -7.11) * mm});
            skArc(sketch, "E6.63.0", {"start": v(-6, -6.22) * mm, "mid": v(-5.91, -6.3) * mm, "end": v(-5.83, -6.37) * mm});
            skLineSegment(sketch, "E6.63.1", {"start": v(-5.83, -6.37) * mm, "end": v(-7.11, -7.78) * mm});
            skArc(sketch, "E6.63.2", {"start": v(-7.32, -7.59) * mm, "mid": v(-7.22, -7.68) * mm, "end": v(-7.11, -7.78) * mm});
            skLineSegment(sketch, "E6.63.3", {"start": v(-6, -6.22) * mm, "end": v(-7.32, -7.59) * mm});
            skArc(sketch, "E6.64.0", {"start": v(-5.6, -6.58) * mm, "mid": v(-5.5, -6.65) * mm, "end": v(-5.42, -6.73) * mm});
            skLineSegment(sketch, "E6.64.1", {"start": v(-5.42, -6.73) * mm, "end": v(-6.61, -8.2) * mm});
            skArc(sketch, "E6.64.2", {"start": v(-6.82, -8.03) * mm, "mid": v(-6.72, -8.12) * mm, "end": v(-6.61, -8.2) * mm});
            skLineSegment(sketch, "E6.64.3", {"start": v(-5.6, -6.58) * mm, "end": v(-6.82, -8.03) * mm});
            skArc(sketch, "E6.65.0", {"start": v(-5.17, -6.92) * mm, "mid": v(-5.08, -6.99) * mm, "end": v(-4.98, -7.05) * mm});
            skLineSegment(sketch, "E6.65.1", {"start": v(-4.98, -7.05) * mm, "end": v(-6.08, -8.6) * mm});
            skArc(sketch, "E6.65.2", {"start": v(-6.3, -8.45) * mm, "mid": v(-6.2, -8.53) * mm, "end": v(-6.08, -8.6) * mm});
            skLineSegment(sketch, "E6.65.3", {"start": v(-5.17, -6.92) * mm, "end": v(-6.3, -8.45) * mm});
            skArc(sketch, "E6.66.0", {"start": v(-4.72, -7.23) * mm, "mid": v(-4.63, -7.3) * mm, "end": v(-4.53, -7.35) * mm});
            skLineSegment(sketch, "E6.66.1", {"start": v(-4.53, -7.35) * mm, "end": v(-5.53, -8.97) * mm});
            skArc(sketch, "E6.66.2", {"start": v(-5.76, -8.83) * mm, "mid": v(-5.65, -8.9) * mm, "end": v(-5.53, -8.97) * mm});
            skLineSegment(sketch, "E6.66.3", {"start": v(-4.72, -7.23) * mm, "end": v(-5.76, -8.83) * mm});
            skArc(sketch, "E6.67.0", {"start": v(-4.26, -7.51) * mm, "mid": v(-4.16, -7.57) * mm, "end": v(-4.06, -7.62) * mm});
            skLineSegment(sketch, "E6.67.1", {"start": v(-4.06, -7.62) * mm, "end": v(-4.96, -9.3) * mm});
            skArc(sketch, "E6.67.2", {"start": v(-5.2, -9.17) * mm, "mid": v(-5.08, -9.24) * mm, "end": v(-4.96, -9.3) * mm});
            skLineSegment(sketch, "E6.67.3", {"start": v(-4.26, -7.51) * mm, "end": v(-5.2, -9.17) * mm});
            skArc(sketch, "E6.68.0", {"start": v(-3.78, -7.77) * mm, "mid": v(-3.68, -7.81) * mm, "end": v(-3.57, -7.86) * mm});
            skLineSegment(sketch, "E6.68.1", {"start": v(-3.57, -7.86) * mm, "end": v(-4.36, -9.6) * mm});
            skArc(sketch, "E6.68.2", {"start": v(-4.61, -9.48) * mm, "mid": v(-4.49, -9.54) * mm, "end": v(-4.36, -9.6) * mm});
            skLineSegment(sketch, "E6.68.3", {"start": v(-3.78, -7.77) * mm, "end": v(-4.61, -9.48) * mm});
            skArc(sketch, "E6.69.0", {"start": v(-3.28, -7.99) * mm, "mid": v(-3.18, -8.03) * mm, "end": v(-3.07, -8.07) * mm});
            skLineSegment(sketch, "E6.69.1", {"start": v(-3.07, -8.07) * mm, "end": v(-3.75, -9.85) * mm});
            skArc(sketch, "E6.69.2", {"start": v(-4, -9.75) * mm, "mid": v(-3.88, -9.8) * mm, "end": v(-3.75, -9.85) * mm});
            skLineSegment(sketch, "E6.69.3", {"start": v(-3.28, -7.99) * mm, "end": v(-4, -9.75) * mm});
            skArc(sketch, "E6.70.0", {"start": v(-2.78, -8.18) * mm, "mid": v(-2.67, -8.21) * mm, "end": v(-2.56, -8.25) * mm});
            skLineSegment(sketch, "E6.70.1", {"start": v(-2.56, -8.25) * mm, "end": v(-3.13, -10.07) * mm});
            skArc(sketch, "E6.70.2", {"start": v(-3.39, -9.98) * mm, "mid": v(-3.26, -10.03) * mm, "end": v(-3.13, -10.07) * mm});
            skLineSegment(sketch, "E6.70.3", {"start": v(-2.78, -8.18) * mm, "end": v(-3.39, -9.98) * mm});
            skArc(sketch, "E6.71.0", {"start": v(-2.26, -8.34) * mm, "mid": v(-2.15, -8.36) * mm, "end": v(-2.04, -8.4) * mm});
            skLineSegment(sketch, "E6.71.1", {"start": v(-2.04, -8.4) * mm, "end": v(-2.49, -10.24) * mm});
            skArc(sketch, "E6.71.2", {"start": v(-2.75, -10.17) * mm, "mid": v(-2.62, -10.2) * mm, "end": v(-2.49, -10.24) * mm});
            skLineSegment(sketch, "E6.71.3", {"start": v(-2.26, -8.34) * mm, "end": v(-2.75, -10.17) * mm});
            skArc(sketch, "E6.72.0", {"start": v(-1.73, -8.46) * mm, "mid": v(-1.62, -8.48) * mm, "end": v(-1.5, -8.5) * mm});
            skLineSegment(sketch, "E6.72.1", {"start": v(-1.5, -8.5) * mm, "end": v(-1.84, -10.38) * mm});
            skArc(sketch, "E6.72.2", {"start": v(-2.11, -10.33) * mm, "mid": v(-1.98, -10.35) * mm, "end": v(-1.84, -10.38) * mm});
            skLineSegment(sketch, "E6.72.3", {"start": v(-1.73, -8.46) * mm, "end": v(-2.11, -10.33) * mm});
            skArc(sketch, "E6.73.0", {"start": v(-1.2, -8.55) * mm, "mid": v(-1.08, -8.57) * mm, "end": v(-0.97, -8.58) * mm});
            skLineSegment(sketch, "E6.73.1", {"start": v(-0.97, -8.58) * mm, "end": v(-1.18, -10.47) * mm});
            skArc(sketch, "E6.73.2", {"start": v(-1.46, -10.44) * mm, "mid": v(-1.32, -10.46) * mm, "end": v(-1.18, -10.47) * mm});
            skLineSegment(sketch, "E6.73.3", {"start": v(-1.2, -8.55) * mm, "end": v(-1.46, -10.44) * mm});
            skArc(sketch, "E6.74.0", {"start": v(-0.66, -8.61) * mm, "mid": v(-0.54, -8.62) * mm, "end": v(-0.43, -8.63) * mm});
            skLineSegment(sketch, "E6.74.1", {"start": v(-0.43, -8.63) * mm, "end": v(-0.52, -10.53) * mm});
            skArc(sketch, "E6.74.2", {"start": v(-0.8, -10.51) * mm, "mid": v(-0.66, -10.52) * mm, "end": v(-0.52, -10.53) * mm});
            skLineSegment(sketch, "E6.74.3", {"start": v(-0.66, -8.61) * mm, "end": v(-0.8, -10.51) * mm});
            skArc(sketch, "E6.75.0", {"start": v(-0.11, -8.64) * mm, "mid": v(0, -8.64) * mm, "end": v(0.11, -8.64) * mm});
            skLineSegment(sketch, "E6.75.1", {"start": v(0.11, -8.64) * mm, "end": v(0.14, -10.54) * mm});
            skArc(sketch, "E6.75.2", {"start": v(-0.14, -10.54) * mm, "mid": v(0, -10.54) * mm, "end": v(0.14, -10.54) * mm});
            skLineSegment(sketch, "E6.75.3", {"start": v(-0.11, -8.64) * mm, "end": v(-0.14, -10.54) * mm});
            skArc(sketch, "E6.76.0", {"start": v(0.43, -8.63) * mm, "mid": v(0.54, -8.62) * mm, "end": v(0.66, -8.61) * mm});
            skLineSegment(sketch, "E6.76.1", {"start": v(0.66, -8.61) * mm, "end": v(0.8, -10.51) * mm});
            skArc(sketch, "E6.76.2", {"start": v(0.52, -10.53) * mm, "mid": v(0.66, -10.52) * mm, "end": v(0.8, -10.51) * mm});
            skLineSegment(sketch, "E6.76.3", {"start": v(0.43, -8.63) * mm, "end": v(0.52, -10.53) * mm});
            skArc(sketch, "E6.77.0", {"start": v(0.97, -8.58) * mm, "mid": v(1.08, -8.57) * mm, "end": v(1.2, -8.55) * mm});
            skLineSegment(sketch, "E6.77.1", {"start": v(1.2, -8.55) * mm, "end": v(1.46, -10.44) * mm});
            skArc(sketch, "E6.77.2", {"start": v(1.18, -10.47) * mm, "mid": v(1.32, -10.46) * mm, "end": v(1.46, -10.44) * mm});
            skLineSegment(sketch, "E6.77.3", {"start": v(0.97, -8.58) * mm, "end": v(1.18, -10.47) * mm});
            skArc(sketch, "E6.78.0", {"start": v(1.5, -8.5) * mm, "mid": v(1.62, -8.48) * mm, "end": v(1.73, -8.46) * mm});
            skLineSegment(sketch, "E6.78.1", {"start": v(1.73, -8.46) * mm, "end": v(2.11, -10.33) * mm});
            skArc(sketch, "E6.78.2", {"start": v(1.84, -10.38) * mm, "mid": v(1.98, -10.35) * mm, "end": v(2.11, -10.33) * mm});
            skLineSegment(sketch, "E6.78.3", {"start": v(1.5, -8.5) * mm, "end": v(1.84, -10.38) * mm});
            skArc(sketch, "E6.79.0", {"start": v(2.04, -8.4) * mm, "mid": v(2.15, -8.36) * mm, "end": v(2.26, -8.34) * mm});
            skLineSegment(sketch, "E6.79.1", {"start": v(2.26, -8.34) * mm, "end": v(2.75, -10.17) * mm});
            skArc(sketch, "E6.79.2", {"start": v(2.49, -10.24) * mm, "mid": v(2.62, -10.2) * mm, "end": v(2.75, -10.17) * mm});
            skLineSegment(sketch, "E6.79.3", {"start": v(2.04, -8.4) * mm, "end": v(2.49, -10.24) * mm});
            skArc(sketch, "E6.80.0", {"start": v(2.56, -8.25) * mm, "mid": v(2.67, -8.21) * mm, "end": v(2.78, -8.18) * mm});
            skLineSegment(sketch, "E6.80.1", {"start": v(2.78, -8.18) * mm, "end": v(3.39, -9.98) * mm});
            skArc(sketch, "E6.80.2", {"start": v(3.13, -10.07) * mm, "mid": v(3.26, -10.03) * mm, "end": v(3.39, -9.98) * mm});
            skLineSegment(sketch, "E6.80.3", {"start": v(2.56, -8.25) * mm, "end": v(3.13, -10.07) * mm});
            skArc(sketch, "E6.81.0", {"start": v(3.07, -8.07) * mm, "mid": v(3.18, -8.03) * mm, "end": v(3.28, -7.99) * mm});
            skLineSegment(sketch, "E6.81.1", {"start": v(3.28, -7.99) * mm, "end": v(4, -9.75) * mm});
            skArc(sketch, "E6.81.2", {"start": v(3.75, -9.85) * mm, "mid": v(3.88, -9.8) * mm, "end": v(4, -9.75) * mm});
            skLineSegment(sketch, "E6.81.3", {"start": v(3.07, -8.07) * mm, "end": v(3.75, -9.85) * mm});
            skArc(sketch, "E6.82.0", {"start": v(3.57, -7.86) * mm, "mid": v(3.68, -7.81) * mm, "end": v(3.78, -7.77) * mm});
            skLineSegment(sketch, "E6.82.1", {"start": v(3.78, -7.77) * mm, "end": v(4.61, -9.48) * mm});
            skArc(sketch, "E6.82.2", {"start": v(4.36, -9.6) * mm, "mid": v(4.49, -9.54) * mm, "end": v(4.61, -9.48) * mm});
            skLineSegment(sketch, "E6.82.3", {"start": v(3.57, -7.86) * mm, "end": v(4.36, -9.6) * mm});
            skArc(sketch, "E6.83.0", {"start": v(4.06, -7.62) * mm, "mid": v(4.16, -7.57) * mm, "end": v(4.26, -7.51) * mm});
            skLineSegment(sketch, "E6.83.1", {"start": v(4.26, -7.51) * mm, "end": v(5.2, -9.17) * mm});
            skArc(sketch, "E6.83.2", {"start": v(4.96, -9.3) * mm, "mid": v(5.08, -9.24) * mm, "end": v(5.2, -9.17) * mm});
            skLineSegment(sketch, "E6.83.3", {"start": v(4.06, -7.62) * mm, "end": v(4.96, -9.3) * mm});
            skArc(sketch, "E6.84.0", {"start": v(4.53, -7.35) * mm, "mid": v(4.63, -7.3) * mm, "end": v(4.72, -7.23) * mm});
            skLineSegment(sketch, "E6.84.1", {"start": v(4.72, -7.23) * mm, "end": v(5.76, -8.83) * mm});
            skArc(sketch, "E6.84.2", {"start": v(5.53, -8.97) * mm, "mid": v(5.65, -8.9) * mm, "end": v(5.76, -8.83) * mm});
            skLineSegment(sketch, "E6.84.3", {"start": v(4.53, -7.35) * mm, "end": v(5.53, -8.97) * mm});
            skArc(sketch, "E6.85.0", {"start": v(4.98, -7.05) * mm, "mid": v(5.08, -6.99) * mm, "end": v(5.17, -6.92) * mm});
            skLineSegment(sketch, "E6.85.1", {"start": v(5.17, -6.92) * mm, "end": v(6.3, -8.45) * mm});
            skArc(sketch, "E6.85.2", {"start": v(6.08, -8.6) * mm, "mid": v(6.2, -8.53) * mm, "end": v(6.3, -8.45) * mm});
            skLineSegment(sketch, "E6.85.3", {"start": v(4.98, -7.05) * mm, "end": v(6.08, -8.6) * mm});
            skArc(sketch, "E6.86.0", {"start": v(5.42, -6.73) * mm, "mid": v(5.5, -6.65) * mm, "end": v(5.6, -6.58) * mm});
            skLineSegment(sketch, "E6.86.1", {"start": v(5.6, -6.58) * mm, "end": v(6.82, -8.03) * mm});
            skArc(sketch, "E6.86.2", {"start": v(6.61, -8.2) * mm, "mid": v(6.72, -8.12) * mm, "end": v(6.82, -8.03) * mm});
            skLineSegment(sketch, "E6.86.3", {"start": v(5.42, -6.73) * mm, "end": v(6.61, -8.2) * mm});
            skArc(sketch, "E6.87.0", {"start": v(5.83, -6.37) * mm, "mid": v(5.91, -6.3) * mm, "end": v(6, -6.22) * mm});
            skLineSegment(sketch, "E6.87.1", {"start": v(6, -6.22) * mm, "end": v(7.32, -7.59) * mm});
            skArc(sketch, "E6.87.2", {"start": v(7.11, -7.78) * mm, "mid": v(7.22, -7.68) * mm, "end": v(7.32, -7.59) * mm});
            skLineSegment(sketch, "E6.87.3", {"start": v(5.83, -6.37) * mm, "end": v(7.11, -7.78) * mm});
            skArc(sketch, "E6.88.0", {"start": v(6.22, -6) * mm, "mid": v(6.3, -5.91) * mm, "end": v(6.37, -5.83) * mm});
            skLineSegment(sketch, "E6.88.1", {"start": v(6.37, -5.83) * mm, "end": v(7.78, -7.11) * mm});
            skArc(sketch, "E6.88.2", {"start": v(7.59, -7.32) * mm, "mid": v(7.68, -7.22) * mm, "end": v(7.78, -7.11) * mm});
            skLineSegment(sketch, "E6.88.3", {"start": v(6.22, -6) * mm, "end": v(7.59, -7.32) * mm});
            skArc(sketch, "E6.89.0", {"start": v(6.58, -5.6) * mm, "mid": v(6.65, -5.5) * mm, "end": v(6.73, -5.42) * mm});
            skLineSegment(sketch, "E6.89.1", {"start": v(6.73, -5.42) * mm, "end": v(8.2, -6.61) * mm});
            skArc(sketch, "E6.89.2", {"start": v(8.03, -6.82) * mm, "mid": v(8.12, -6.72) * mm, "end": v(8.2, -6.61) * mm});
            skLineSegment(sketch, "E6.89.3", {"start": v(6.58, -5.6) * mm, "end": v(8.03, -6.82) * mm});
            skArc(sketch, "E6.90.0", {"start": v(6.92, -5.17) * mm, "mid": v(6.99, -5.08) * mm, "end": v(7.05, -4.98) * mm});
            skLineSegment(sketch, "E6.90.1", {"start": v(7.05, -4.98) * mm, "end": v(8.6, -6.08) * mm});
            skArc(sketch, "E6.90.2", {"start": v(8.45, -6.3) * mm, "mid": v(8.53, -6.2) * mm, "end": v(8.6, -6.08) * mm});
            skLineSegment(sketch, "E6.90.3", {"start": v(6.92, -5.17) * mm, "end": v(8.45, -6.3) * mm});
            skArc(sketch, "E6.91.0", {"start": v(7.23, -4.72) * mm, "mid": v(7.3, -4.63) * mm, "end": v(7.35, -4.53) * mm});
            skLineSegment(sketch, "E6.91.1", {"start": v(7.35, -4.53) * mm, "end": v(8.97, -5.53) * mm});
            skArc(sketch, "E6.91.2", {"start": v(8.83, -5.76) * mm, "mid": v(8.9, -5.65) * mm, "end": v(8.97, -5.53) * mm});
            skLineSegment(sketch, "E6.91.3", {"start": v(7.23, -4.72) * mm, "end": v(8.83, -5.76) * mm});
            skArc(sketch, "E6.92.0", {"start": v(7.51, -4.26) * mm, "mid": v(7.57, -4.16) * mm, "end": v(7.62, -4.06) * mm});
            skLineSegment(sketch, "E6.92.1", {"start": v(7.62, -4.06) * mm, "end": v(9.3, -4.96) * mm});
            skArc(sketch, "E6.92.2", {"start": v(9.17, -5.2) * mm, "mid": v(9.24, -5.08) * mm, "end": v(9.3, -4.96) * mm});
            skLineSegment(sketch, "E6.92.3", {"start": v(7.51, -4.26) * mm, "end": v(9.17, -5.2) * mm});
            skArc(sketch, "E6.93.0", {"start": v(7.77, -3.78) * mm, "mid": v(7.81, -3.68) * mm, "end": v(7.86, -3.57) * mm});
            skLineSegment(sketch, "E6.93.1", {"start": v(7.86, -3.57) * mm, "end": v(9.6, -4.36) * mm});
            skArc(sketch, "E6.93.2", {"start": v(9.48, -4.61) * mm, "mid": v(9.54, -4.49) * mm, "end": v(9.6, -4.36) * mm});
            skLineSegment(sketch, "E6.93.3", {"start": v(7.77, -3.78) * mm, "end": v(9.48, -4.61) * mm});
            skArc(sketch, "E6.94.0", {"start": v(7.99, -3.28) * mm, "mid": v(8.03, -3.18) * mm, "end": v(8.07, -3.07) * mm});
            skLineSegment(sketch, "E6.94.1", {"start": v(8.07, -3.07) * mm, "end": v(9.85, -3.75) * mm});
            skArc(sketch, "E6.94.2", {"start": v(9.75, -4) * mm, "mid": v(9.8, -3.88) * mm, "end": v(9.85, -3.75) * mm});
            skLineSegment(sketch, "E6.94.3", {"start": v(7.99, -3.28) * mm, "end": v(9.75, -4) * mm});
            skArc(sketch, "E6.95.0", {"start": v(8.18, -2.78) * mm, "mid": v(8.21, -2.67) * mm, "end": v(8.25, -2.56) * mm});
            skLineSegment(sketch, "E6.95.1", {"start": v(8.25, -2.56) * mm, "end": v(10.07, -3.13) * mm});
            skArc(sketch, "E6.95.2", {"start": v(9.98, -3.39) * mm, "mid": v(10.03, -3.26) * mm, "end": v(10.07, -3.13) * mm});
            skLineSegment(sketch, "E6.95.3", {"start": v(8.18, -2.78) * mm, "end": v(9.98, -3.39) * mm});
            skArc(sketch, "E6.96.0", {"start": v(8.34, -2.26) * mm, "mid": v(8.36, -2.15) * mm, "end": v(8.4, -2.04) * mm});
            skLineSegment(sketch, "E6.96.1", {"start": v(8.4, -2.04) * mm, "end": v(10.24, -2.49) * mm});
            skArc(sketch, "E6.96.2", {"start": v(10.17, -2.75) * mm, "mid": v(10.2, -2.62) * mm, "end": v(10.24, -2.49) * mm});
            skLineSegment(sketch, "E6.96.3", {"start": v(8.34, -2.26) * mm, "end": v(10.17, -2.75) * mm});
            skArc(sketch, "E6.97.0", {"start": v(8.46, -1.73) * mm, "mid": v(8.48, -1.62) * mm, "end": v(8.5, -1.5) * mm});
            skLineSegment(sketch, "E6.97.1", {"start": v(8.5, -1.5) * mm, "end": v(10.38, -1.84) * mm});
            skArc(sketch, "E6.97.2", {"start": v(10.33, -2.11) * mm, "mid": v(10.35, -1.98) * mm, "end": v(10.38, -1.84) * mm});
            skLineSegment(sketch, "E6.97.3", {"start": v(8.46, -1.73) * mm, "end": v(10.33, -2.11) * mm});
            skArc(sketch, "E6.98.0", {"start": v(8.55, -1.2) * mm, "mid": v(8.57, -1.08) * mm, "end": v(8.58, -0.97) * mm});
            skLineSegment(sketch, "E6.98.1", {"start": v(8.58, -0.97) * mm, "end": v(10.47, -1.18) * mm});
            skArc(sketch, "E6.98.2", {"start": v(10.44, -1.46) * mm, "mid": v(10.46, -1.32) * mm, "end": v(10.47, -1.18) * mm});
            skLineSegment(sketch, "E6.98.3", {"start": v(8.55, -1.2) * mm, "end": v(10.44, -1.46) * mm});
            skArc(sketch, "E6.99.0", {"start": v(8.61, -0.66) * mm, "mid": v(8.62, -0.54) * mm, "end": v(8.63, -0.43) * mm});
            skLineSegment(sketch, "E6.99.1", {"start": v(8.63, -0.43) * mm, "end": v(10.53, -0.52) * mm});
            skArc(sketch, "E6.99.2", {"start": v(10.51, -0.8) * mm, "mid": v(10.52, -0.66) * mm, "end": v(10.53, -0.52) * mm});
            skLineSegment(sketch, "E6.99.3", {"start": v(8.61, -0.66) * mm, "end": v(10.51, -0.8) * mm});
            skSolve(sketch);
        }
        {
            var Q0;
            Q0 = qSketchRegion(id + "F3", true);
            extrude(context, id + "F4", {"entities" : qUnion([Q0]), "operationType" : NewBodyOperationType.REMOVE, "oppositeDirection" : true, "depth" : 25.4 * mm});
        }
    });
